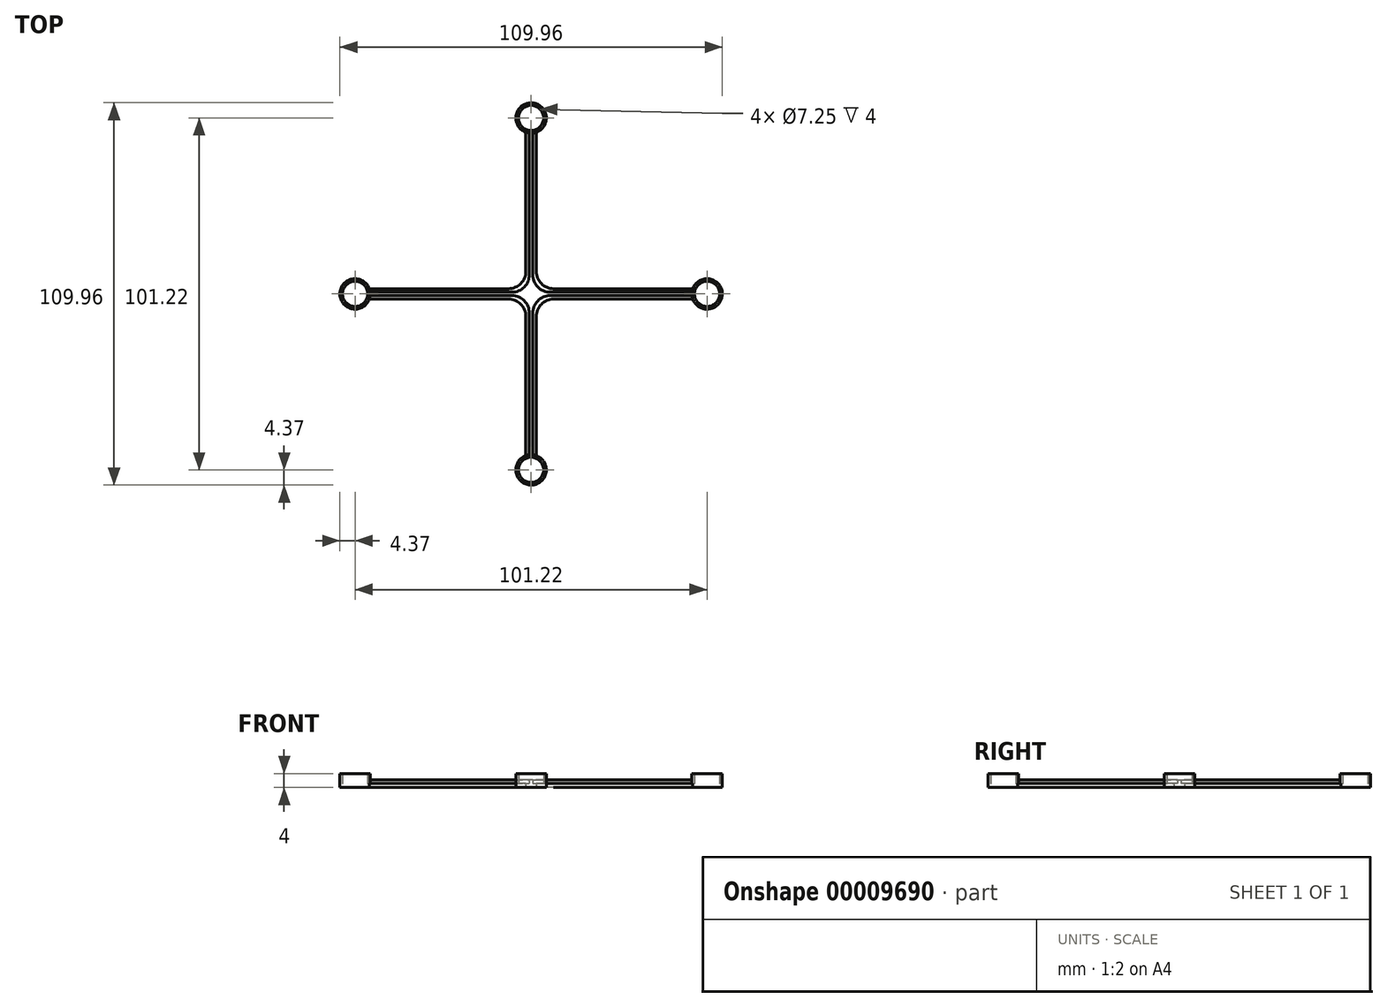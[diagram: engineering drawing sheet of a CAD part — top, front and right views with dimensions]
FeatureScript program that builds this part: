
annotation { "Feature Type Name" : "Feature", "Feature Type Description" : "" }
export const myFeature = defineFeature(function(context is Context, id is Id, definition is map)
    precondition{}
    {
        {
            var Q0;
            Q0=qCreatedBy(makeId("Top.planeOp"),FACE);
            var sketch = newSketch(context, id + "F0", { "sketchPlane" : qUnion([Q0])});
            skCircle(sketch, "E0", {"center": v(-50.6, 0) * mm, "radius": 3.62 * mm});
            skCircle(sketch, "E1", {"center": v(-50.6, 0) * mm, "radius": 4.38 * mm});
            skCircle(sketch, "E2.1.0", {"center": v(0, -50.6) * mm, "radius": 3.62 * mm});
            skCircle(sketch, "E2.1.1", {"center": v(0, -50.6) * mm, "radius": 4.38 * mm});
            skCircle(sketch, "E2.2.0", {"center": v(50.6, 0) * mm, "radius": 3.62 * mm});
            skCircle(sketch, "E2.2.1", {"center": v(50.6, 0) * mm, "radius": 4.38 * mm});
            skCircle(sketch, "E2.3.0", {"center": v(0, 50.6) * mm, "radius": 3.62 * mm});
            skCircle(sketch, "E2.3.1", {"center": v(0, 50.6) * mm, "radius": 4.38 * mm});
            skPoint(sketch, "E2.center", {"position": v(0, 0) * mm});
            skLineSegment(sketch, "E3", {"start": v(-46.5, 1.5) * mm, "end": v(-6.5, 1.5) * mm});
            skLineSegment(sketch, "E4", {"start": v(-1.5, 6.5) * mm, "end": v(-1.5, 46.5) * mm});
            skLineSegment(sketch, "E5.1.0", {"start": v(-6.5, -1.5) * mm, "end": v(-46.5, -1.5) * mm});
            skLineSegment(sketch, "E5.1.2", {"start": v(-1.5, -46.5) * mm, "end": v(-1.5, -6.5) * mm});
            skLineSegment(sketch, "E5.2.0", {"start": v(1.5, -6.5) * mm, "end": v(1.5, -46.5) * mm});
            skLineSegment(sketch, "E5.2.2", {"start": v(46.5, -1.5) * mm, "end": v(6.5, -1.5) * mm});
            skLineSegment(sketch, "E5.3.0", {"start": v(6.5, 1.5) * mm, "end": v(46.5, 1.5) * mm});
            skLineSegment(sketch, "E5.3.2", {"start": v(1.5, 46.5) * mm, "end": v(1.5, 6.5) * mm});
            skPoint(sketch, "E6.visualSharp", {"position": v(-1.5, -1.5) * mm});
            skArc(sketch, "E6.filletArc", {"start": v(-1.5, -6.5) * mm, "mid": v(-2.96, -2.96) * mm, "end": v(-6.5, -1.5) * mm});
            skPoint(sketch, "E7.visualSharp", {"position": v(-1.5, 1.5) * mm});
            skArc(sketch, "E7.filletArc", {"start": v(-6.5, 1.5) * mm, "mid": v(-2.96, 2.96) * mm, "end": v(-1.5, 6.5) * mm});
            skPoint(sketch, "E8.visualSharp", {"position": v(1.5, 1.5) * mm});
            skArc(sketch, "E8.filletArc", {"start": v(1.5, 6.5) * mm, "mid": v(2.96, 2.96) * mm, "end": v(6.5, 1.5) * mm});
            skPoint(sketch, "E9.visualSharp", {"position": v(1.5, -1.5) * mm});
            skArc(sketch, "E9.filletArc", {"start": v(6.5, -1.5) * mm, "mid": v(2.96, -2.96) * mm, "end": v(1.5, -6.5) * mm});
            skSolve(sketch);
        }
        {
            var Q0;
            Q0=qSketchRegion(id+"F0",true);
            var Q1;
            {var subQ3=sQuery(id+"F0.wireOp",EDGE,"E5.3.1");Q1=makeQuery(id+"F0.imprint","IMPRINT",FACE,{"disambiguationData":[TD([[makeQuery(id+"F0.imprint","IMPRINT",EDGE,{"derivedFrom":subQ3}),-1.0]])]});}
            var Q2;
            {var subQ3=sQuery(id+"F0.wireOp",EDGE,"112c20ca-e4e8-40d7-89ba-900f44e64bb5");Q2=makeQuery(id+"F0.imprint","IMPRINT",FACE,{"disambiguationData":[TD([[makeQuery(id+"F0.imprint","IMPRINT",EDGE,{"derivedFrom":subQ3}),-1.0]])]});}
            var Q3;
            {var subQ3=sQuery(id+"F0.wireOp",EDGE,"E5.1.1");Q3=makeQuery(id+"F0.imprint","IMPRINT",FACE,{"disambiguationData":[TD([[makeQuery(id+"F0.imprint","IMPRINT",EDGE,{"derivedFrom":subQ3}),-1.0]])]});}
            var Q4;
            {var subQ3=sQuery(id+"F0.wireOp",EDGE,"E5.2.1");Q4=makeQuery(id+"F0.imprint","IMPRINT",FACE,{"disambiguationData":[TD([[makeQuery(id+"F0.imprint","IMPRINT",EDGE,{"derivedFrom":subQ3}),-1.0]])]});}
            extrude(context, id + "F1", {"entities" : qUnion([Q0, Q1, Q2, Q3, Q4]), "depth" : 1.25 * mm});
        }
        {
            var Q0;
            Q0=makeQuery(id+"F1.opExtrude","CAP_FACE",FACE,{"disambiguationData":[OSD([sQuery(id+"F0.wireOp",EDGE,"E0"),sQuery(id+"F0.wireOp",EDGE,"E1"),sQuery(id+"F0.wireOp",EDGE,"E2.1.0"),sQuery(id+"F0.wireOp",EDGE,"E2.1.1"),sQuery(id+"F0.wireOp",EDGE,"E2.2.0"),sQuery(id+"F0.wireOp",EDGE,"E2.2.1"),sQuery(id+"F0.wireOp",EDGE,"E2.3.0"),sQuery(id+"F0.wireOp",EDGE,"E2.3.1"),sQuery(id+"F0.wireOp",EDGE,"E3"),sQuery(id+"F0.wireOp",EDGE,"E4"),sQuery(id+"F0.wireOp",EDGE,"E5.1.0"),sQuery(id+"F0.wireOp",EDGE,"E5.1.2"),sQuery(id+"F0.wireOp",EDGE,"E5.2.0"),sQuery(id+"F0.wireOp",EDGE,"E5.2.2"),sQuery(id+"F0.wireOp",EDGE,"E5.3.0"),sQuery(id+"F0.wireOp",EDGE,"E5.3.2"),sQuery(id+"F0.wireOp",EDGE,"E6.filletArc"),sQuery(id+"F0.wireOp",EDGE,"E7.filletArc"),sQuery(id+"F0.wireOp",EDGE,"E8.filletArc"),sQuery(id+"F0.wireOp",EDGE,"E9.filletArc")])],"isStart":false});
            var sketch = newSketch(context, id + "F2", { "sketchPlane" : qUnion([Q0])});
            skLineSegment(sketch, "E10.0", {"start": v(-5.5, 0.5) * mm, "end": v(-46.98, 0.5) * mm});
            skLineSegment(sketch, "E11.0.MirrorCS", {"start": v(-5.5, -0.5) * mm, "end": v(-46.98, -0.5) * mm});
            skLineSegment(sketch, "E12", {"start": v(-46.98, 0.5) * mm, "end": v(-46.98, -0.5) * mm});
            skLineSegment(sketch, "E13.1.0", {"start": v(-0.5, -46.98) * mm, "end": v(0.5, -46.98) * mm});
            skLineSegment(sketch, "E13.1.1", {"start": v(-0.5, -5.5) * mm, "end": v(-0.5, -46.98) * mm});
            skLineSegment(sketch, "E13.1.2", {"start": v(0.5, -5.5) * mm, "end": v(0.5, -46.98) * mm});
            skLineSegment(sketch, "E13.2.0", {"start": v(46.98, -0.5) * mm, "end": v(46.98, 0.5) * mm});
            skLineSegment(sketch, "E13.2.1", {"start": v(5.5, -0.5) * mm, "end": v(46.98, -0.5) * mm});
            skLineSegment(sketch, "E13.2.2", {"start": v(5.5, 0.5) * mm, "end": v(46.98, 0.5) * mm});
            skLineSegment(sketch, "E13.3.0", {"start": v(0.5, 46.98) * mm, "end": v(-0.5, 46.98) * mm});
            skLineSegment(sketch, "E13.3.1", {"start": v(0.5, 5.5) * mm, "end": v(0.5, 46.98) * mm});
            skLineSegment(sketch, "E13.3.2", {"start": v(-0.5, 5.5) * mm, "end": v(-0.5, 46.98) * mm});
            skPoint(sketch, "E13.center", {"position": v(0, 0) * mm});
            skPoint(sketch, "E14.orphan", {"position": v(-0.5, 0) * mm});
            skPoint(sketch, "E15.orphan", {"position": v(0, 0.5) * mm});
            skPoint(sketch, "E16.orphan", {"position": v(0.5, 0) * mm});
            skPoint(sketch, "E17.orphan", {"position": v(0, -0.5) * mm});
            skPoint(sketch, "E18.visualSharp", {"position": v(0.5, 0.5) * mm});
            skArc(sketch, "E18.filletArc", {"start": v(0.5, 5.5) * mm, "mid": v(1.96, 1.96) * mm, "end": v(5.5, 0.5) * mm});
            skPoint(sketch, "E19.visualSharp", {"position": v(0.5, -0.5) * mm});
            skArc(sketch, "E19.filletArc", {"start": v(5.5, -0.5) * mm, "mid": v(1.96, -1.96) * mm, "end": v(0.5, -5.5) * mm});
            skPoint(sketch, "E20.visualSharp", {"position": v(-0.5, -0.5) * mm});
            skArc(sketch, "E20.filletArc", {"start": v(-0.5, -5.5) * mm, "mid": v(-1.96, -1.96) * mm, "end": v(-5.5, -0.5) * mm});
            skPoint(sketch, "E21.visualSharp", {"position": v(-0.5, 0.5) * mm});
            skArc(sketch, "E21.filletArc", {"start": v(-5.5, 0.5) * mm, "mid": v(-1.96, 1.96) * mm, "end": v(-0.5, 5.5) * mm});
            skSolve(sketch);
        }
        {
            var Q0;
            Q0 = qSketchRegion(id + "F2", true);
            extrude(context, id + "F3", {"entities" : qUnion([Q0]), "operationType" : NewBodyOperationType.ADD, "depth" : 1 * mm});
        }
        {
            var Q0;
            Q0=makeQuery(id+"F0.imprint","IMPRINT",FACE,{"disambiguationData":[TD([[makeQuery(id+"F0.imprint","IMPRINT",EDGE,{"derivedFrom":sQuery(id+"F0.wireOp",EDGE,"E2.2.0")}),-1.0]])]});
            var Q1;
            Q1=makeQuery(id+"F0.imprint","IMPRINT",FACE,{"disambiguationData":[TD([[makeQuery(id+"F0.imprint","IMPRINT",EDGE,{"derivedFrom":sQuery(id+"F0.wireOp",EDGE,"E2.1.0")}),-1.0]])]});
            var Q2;
            Q2=makeQuery(id+"F0.imprint","IMPRINT",FACE,{"disambiguationData":[TD([[makeQuery(id+"F0.imprint","IMPRINT",EDGE,{"derivedFrom":sQuery(id+"F0.wireOp",EDGE,"E0")}),-1.0]])]});
            var Q3;
            Q3=makeQuery(id+"F0.imprint","IMPRINT",FACE,{"disambiguationData":[TD([[makeQuery(id+"F0.imprint","IMPRINT",EDGE,{"derivedFrom":sQuery(id+"F0.wireOp",EDGE,"E2.3.0")}),-1.0]])]});
            extrude(context, id + "F4", {"entities" : qUnion([Q0, Q1, Q2, Q3]), "operationType" : NewBodyOperationType.ADD, "depth" : 4 * mm});
        }
    });
